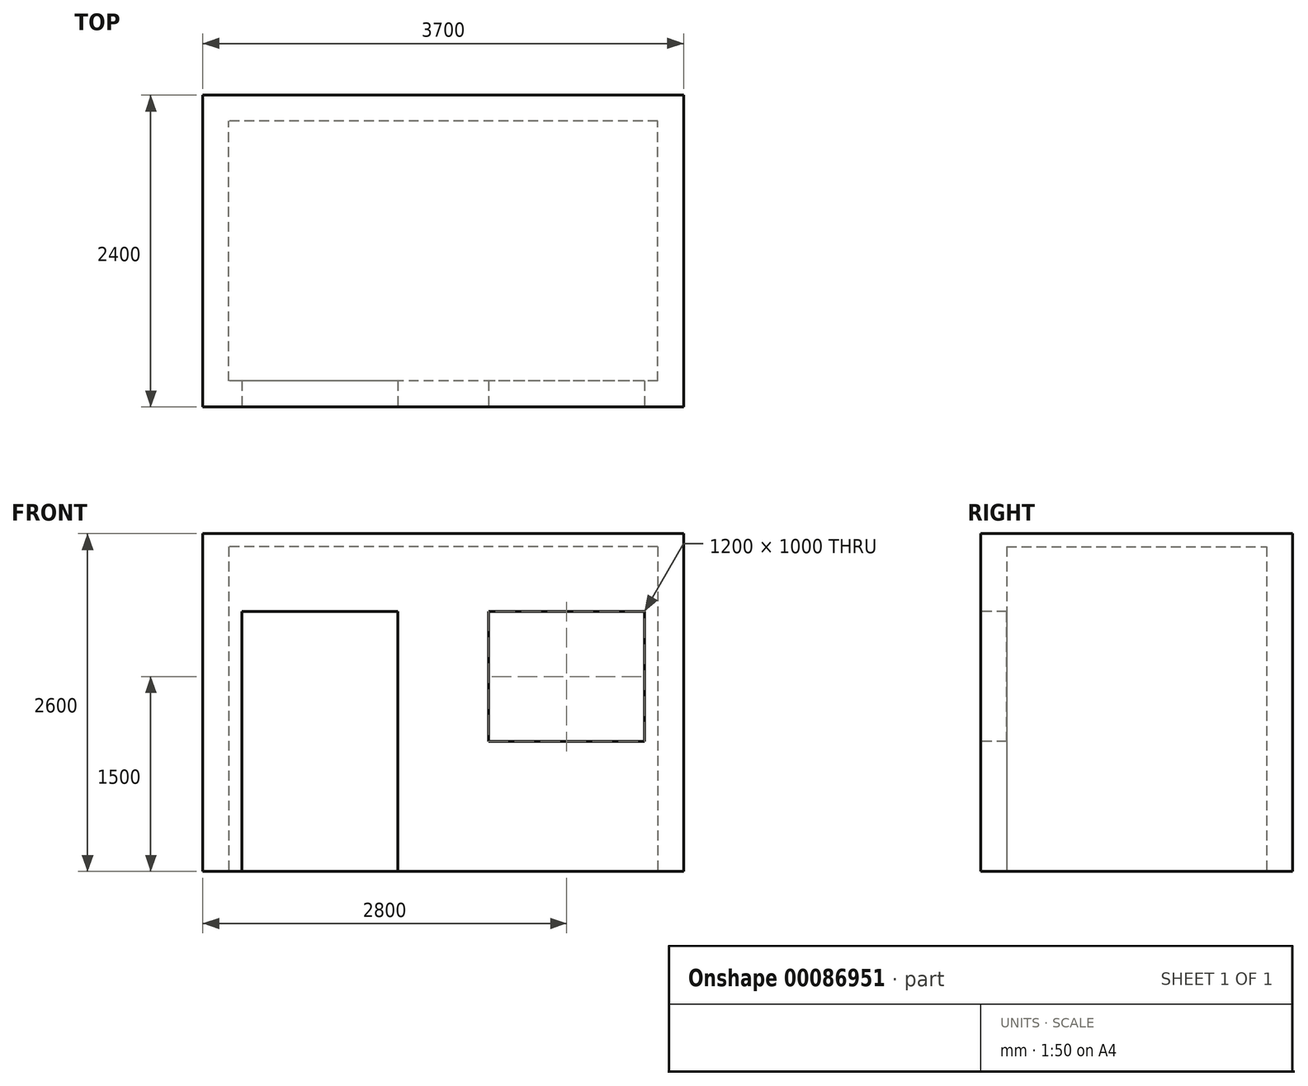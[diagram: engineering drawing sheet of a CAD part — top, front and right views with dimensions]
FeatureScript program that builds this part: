
annotation { "Feature Type Name" : "Feature", "Feature Type Description" : "" }
export const myFeature = defineFeature(function(context is Context, id is Id, definition is map)
    precondition{}
    {
        {
            var Q0;
            Q0=qCreatedBy(makeId("Top.planeOp"),FACE);
            var sketch = newSketch(context, id + "F0", { "sketchPlane" : qUnion([Q0])});
            skLineSegment(sketch, "E0.bottom", {"start": v(1650, -1000) * mm, "end": v(-1650, -1000) * mm});
            skLineSegment(sketch, "E0.top", {"start": v(1650, 1000) * mm, "end": v(-1650, 1000) * mm});
            skLineSegment(sketch, "E0.left", {"start": v(1650, -1000) * mm, "end": v(1650, 1000) * mm});
            skLineSegment(sketch, "E0.right", {"start": v(-1650, -1000) * mm, "end": v(-1650, 1000) * mm});
            skPoint(sketch, "E0.middle", {"position": v(0, 0) * mm});
            skLineSegment(sketch, "E1.bottom", {"start": v(-1850, -1200) * mm, "end": v(1850, -1200) * mm});
            skLineSegment(sketch, "E1.top", {"start": v(-1850, 1200) * mm, "end": v(1850, 1200) * mm});
            skLineSegment(sketch, "E1.left", {"start": v(-1850, -1200) * mm, "end": v(-1850, 1200) * mm});
            skLineSegment(sketch, "E1.right", {"start": v(1850, -1200) * mm, "end": v(1850, 1200) * mm});
            skSolve(sketch);
        }
        {
            var Q0;
            Q0 = qSketchRegion(id + "F0", true);
            extrude(context, id + "F1", {"entities" : qUnion([Q0]), "depth" : 2500 * mm});
        }
        {
            var Q0;
            Q0=makeQuery(id+"F1.opExtrude","CAP_FACE",FACE,{"disambiguationData":[OSD([sQuery(id+"F0.wireOp",EDGE,"E0.bottom"),sQuery(id+"F0.wireOp",EDGE,"E0.top"),sQuery(id+"F0.wireOp",EDGE,"E0.left"),sQuery(id+"F0.wireOp",EDGE,"E0.right"),sQuery(id+"F0.wireOp",EDGE,"E1.bottom"),sQuery(id+"F0.wireOp",EDGE,"E1.top"),sQuery(id+"F0.wireOp",EDGE,"E1.left"),sQuery(id+"F0.wireOp",EDGE,"E1.right")])],"isStart":false});
            var sketch = newSketch(context, id + "F2", { "sketchPlane" : qUnion([Q0])});
            skLineSegment(sketch, "E2.bottom", {"start": v(-1850, 1200) * mm, "end": v(1850, 1200) * mm});
            skLineSegment(sketch, "E2.top", {"start": v(-1850, -1200) * mm, "end": v(1850, -1200) * mm});
            skLineSegment(sketch, "E2.left", {"start": v(-1850, 1200) * mm, "end": v(-1850, -1200) * mm});
            skLineSegment(sketch, "E2.right", {"start": v(1850, 1200) * mm, "end": v(1850, -1200) * mm});
            skSolve(sketch);
        }
        {
            var Q0;
            Q0 = qSketchRegion(id + "F2", true);
            extrude(context, id + "F3", {"entities" : qUnion([Q0]), "operationType" : NewBodyOperationType.ADD, "depth" : 100 * mm});
        }
        {
            var Q0;
            Q0=makeQuery(id+"F3.boolean.opBoolean","MERGE",FACE,{"derivedFrom":[makeQuery(id+"F1.opExtrude","SWEPT_FACE",FACE,{"disambiguationData":[OSD([sQuery(id+"F0.wireOp",EDGE,"E1.bottom")])]}),makeQuery(id+"F3.opExtrude","SWEPT_FACE",FACE,{"disambiguationData":[OSD([sQuery(id+"F2.wireOp",EDGE,"E2.top")])]})]});
            var sketch = newSketch(context, id + "F4", { "sketchPlane" : qUnion([Q0])});
            skLineSegment(sketch, "E3.bottom", {"start": v(-1550, 0) * mm, "end": v(-350, 0) * mm});
            skLineSegment(sketch, "E3.top", {"start": v(-1550, 2000) * mm, "end": v(-350, 2000) * mm});
            skLineSegment(sketch, "E3.left", {"start": v(-1550, 0) * mm, "end": v(-1550, 2000) * mm});
            skLineSegment(sketch, "E3.right", {"start": v(-350, 0) * mm, "end": v(-350, 2000) * mm});
            skLineSegment(sketch, "E4.bottom", {"start": v(350, 2000) * mm, "end": v(1550, 2000) * mm});
            skLineSegment(sketch, "E4.top", {"start": v(350, 1000) * mm, "end": v(1550, 1000) * mm});
            skLineSegment(sketch, "E4.left", {"start": v(350, 2000) * mm, "end": v(350, 1000) * mm});
            skLineSegment(sketch, "E4.right", {"start": v(1550, 2000) * mm, "end": v(1550, 1000) * mm});
            skSolve(sketch);
        }
        {
            var Q0;
            Q0 = qSketchRegion(id + "F4", true);
            extrude(context, id + "F5", {"entities" : qUnion([Q0]), "operationType" : NewBodyOperationType.REMOVE, "endBound" : BoundingType.UP_TO_NEXT, "oppositeDirection" : true, "depth" : 25 * mm});
        }
    });
